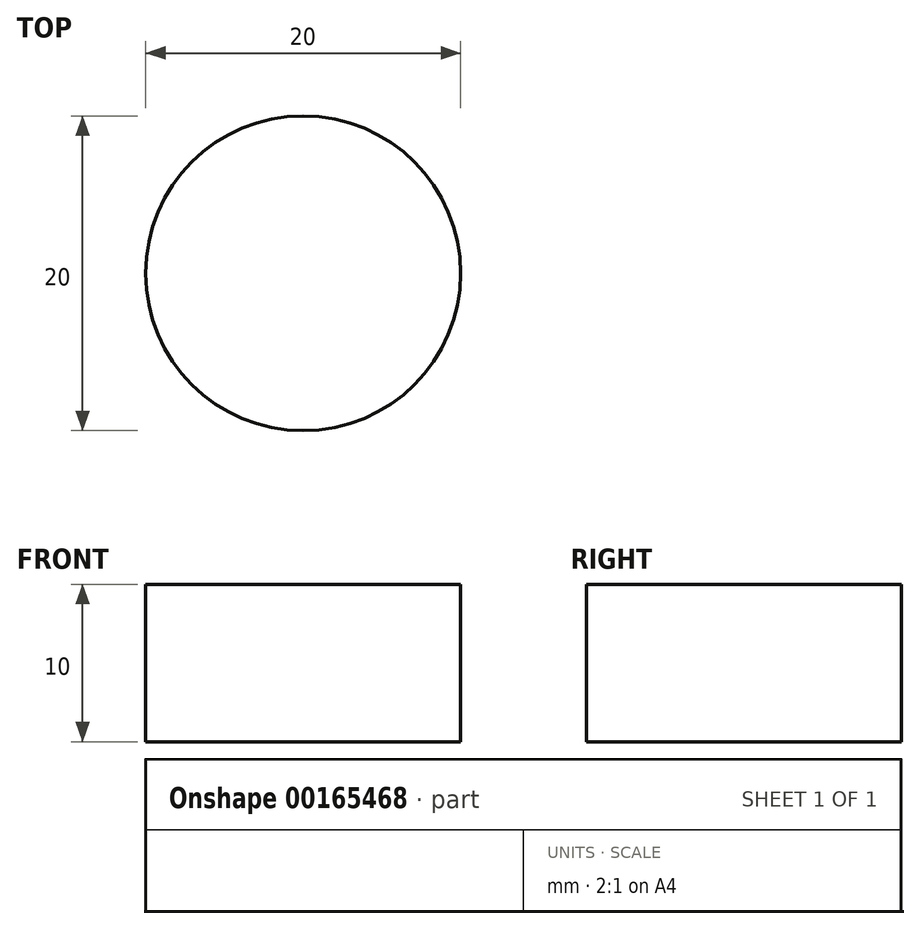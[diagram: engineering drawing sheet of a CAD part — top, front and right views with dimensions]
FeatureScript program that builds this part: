
annotation { "Feature Type Name" : "Feature", "Feature Type Description" : "" }
export const myFeature = defineFeature(function(context is Context, id is Id, definition is map)
    precondition{}
    {
        {
            var Q0;
            Q0=qCreatedBy(makeId("Top.planeOp"),FACE);
            var sketch = newSketch(context, id + "F0", { "sketchPlane" : qUnion([Q0])});
            skCircle(sketch, "E0", {"center": v(0, 0) * mm, "radius": 10 * mm});
            skSolve(sketch);
        }
        {
            var Q0;
            Q0=makeQuery(id+"F0.imprint","IMPRINT",FACE,{"disambiguationData":[TD([[makeQuery(id+"F0.imprint","IMPRINT",EDGE,{"derivedFrom":sQuery(id+"F0.wireOp",EDGE,"E0")}),1.0]])]});
            extrude(context, id + "F1", {"entities" : qUnion([Q0]), "offsetDistance" : 25 * mm, "depth" : 10 * mm});
        }
    });
